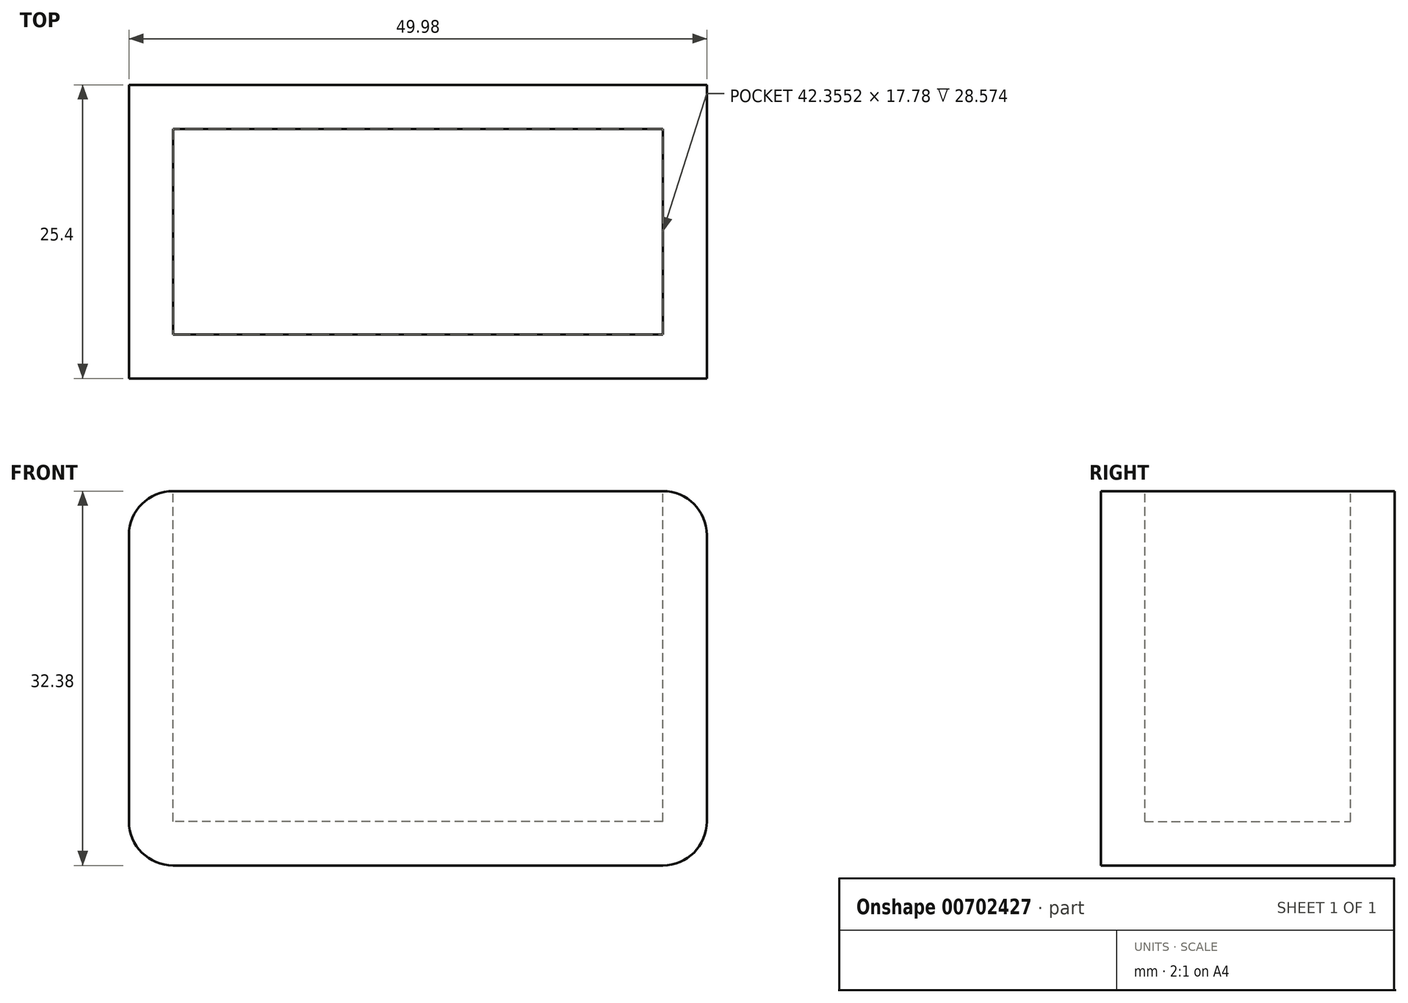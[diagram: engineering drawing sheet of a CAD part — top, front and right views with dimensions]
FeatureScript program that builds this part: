
annotation { "Feature Type Name" : "Feature", "Feature Type Description" : "" }
export const myFeature = defineFeature(function(context is Context, id is Id, definition is map)
    precondition{}
    {
        {
            var Q0;
            Q0=qCreatedBy(makeId("Front.planeOp"),FACE);
            var sketch = newSketch(context, id + "F0", { "sketchPlane" : qUnion([Q0])});
            skLineSegment(sketch, "E0.bottom", {"start": v(21.18, -16.2) * mm, "end": v(-21.18, -16.2) * mm});
            skLineSegment(sketch, "E0.top", {"start": v(21.18, 16.2) * mm, "end": v(-21.18, 16.2) * mm});
            skLineSegment(sketch, "E0.left", {"start": v(24.99, -12.38) * mm, "end": v(24.99, 12.38) * mm});
            skLineSegment(sketch, "E0.right", {"start": v(-24.99, -12.38) * mm, "end": v(-24.99, 12.38) * mm});
            skPoint(sketch, "E0.middle", {"position": v(0, 0) * mm});
            skPoint(sketch, "E1.visualSharp", {"position": v(-24.99, 16.2) * mm});
            skArc(sketch, "E1.filletArc", {"start": v(-21.18, 16.2) * mm, "mid": v(-23.87, 15.08) * mm, "end": v(-24.99, 12.38) * mm});
            skPoint(sketch, "E2.visualSharp", {"position": v(24.99, 16.2) * mm});
            skArc(sketch, "E2.filletArc", {"start": v(24.99, 12.38) * mm, "mid": v(23.87, 15.08) * mm, "end": v(21.18, 16.2) * mm});
            skPoint(sketch, "E3.visualSharp", {"position": v(-24.99, -16.2) * mm});
            skArc(sketch, "E3.filletArc", {"start": v(-24.99, -12.38) * mm, "mid": v(-23.87, -15.08) * mm, "end": v(-21.18, -16.2) * mm});
            skPoint(sketch, "E4.visualSharp", {"position": v(24.99, -16.2) * mm});
            skArc(sketch, "E4.filletArc", {"start": v(21.18, -16.2) * mm, "mid": v(23.87, -15.08) * mm, "end": v(24.99, -12.38) * mm});
            skSolve(sketch);
        }
        {
            var Q0;
            Q0 = qSketchRegion(id + "F0", true);
            extrude(context, id + "F1", {"entities" : qUnion([Q0]), "depth" : 25.4 * mm, "offsetDistance" : 25.4 * mm});
        }
        {
            var Q0;
            Q0=makeQuery(id+"F1.opExtrude","SWEPT_FACE",FACE,{"disambiguationData":[OSD([sQuery(id+"F0.wireOp",EDGE,"E0.top")])]});
            shell(context, id + "F2", {"entities" : qUnion([Q0]), "thickness" : 3.8 * mm});
        }
    });
